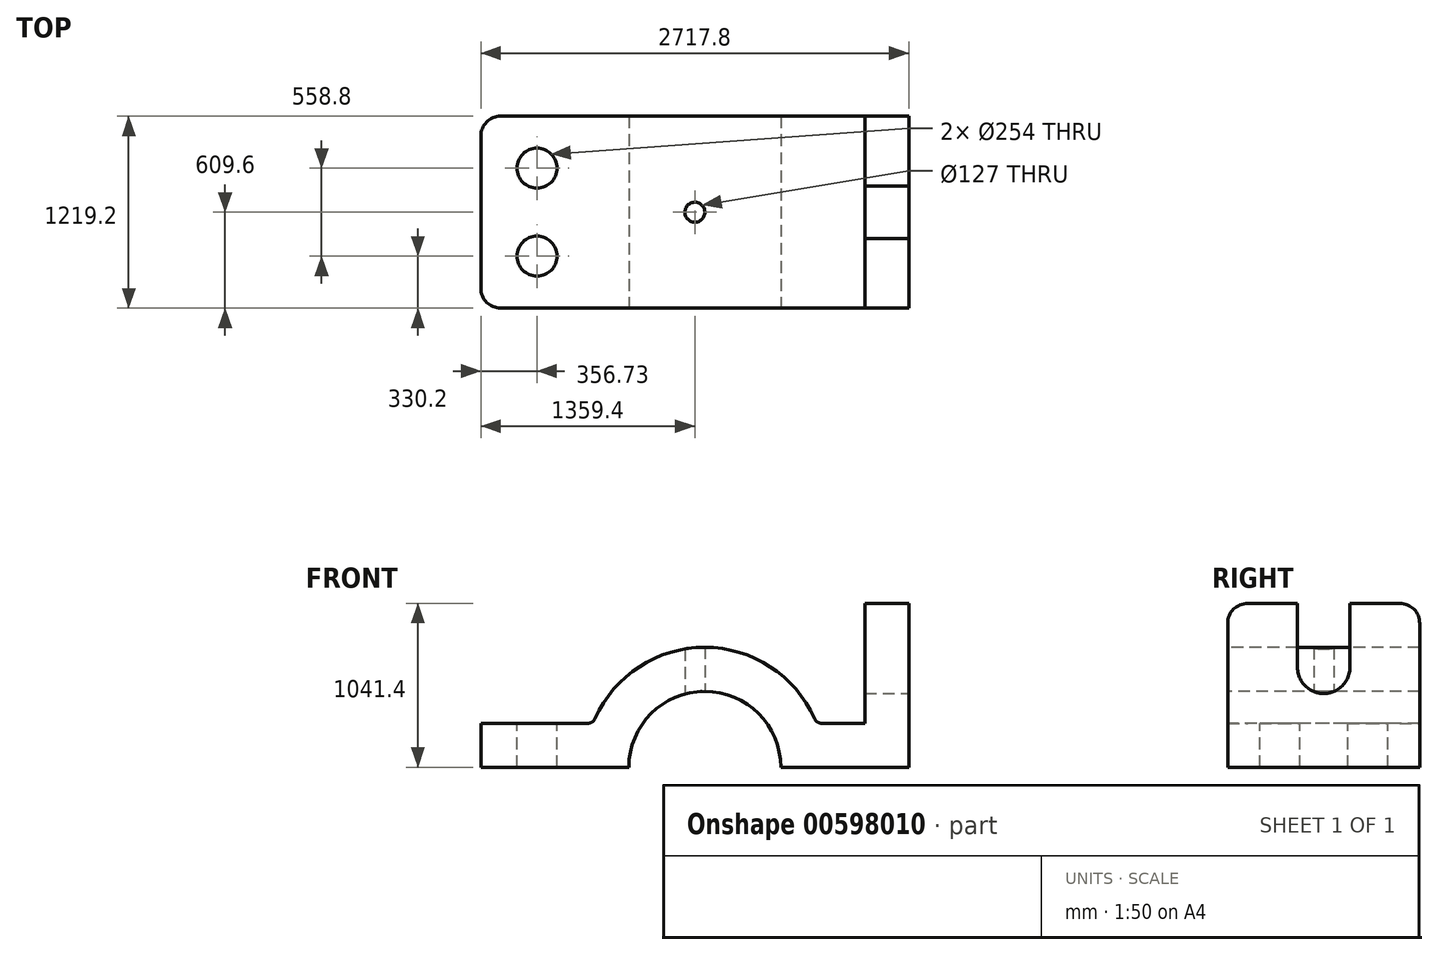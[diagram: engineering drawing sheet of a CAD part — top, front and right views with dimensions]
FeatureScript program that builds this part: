
annotation { "Feature Type Name" : "Feature", "Feature Type Description" : "" }
export const myFeature = defineFeature(function(context is Context, id is Id, definition is map)
    precondition{}
    {
        {
            var Q0;
            Q0=qCreatedBy(makeId("Front.planeOp"),FACE);
            var sketch = newSketch(context, id + "F0", { "sketchPlane" : qUnion([Q0])});
            skLineSegment(sketch, "E0.bottom", {"start": v(-1359.4, -709.05) * mm, "end": v(-419.6, -709.05) * mm});
            skLineSegment(sketch, "E0.top", {"start": v(1079, 332.35) * mm, "end": v(1358.4, 332.35) * mm});
            skLineSegment(sketch, "E0.left", {"start": v(-1359.4, -709.05) * mm, "end": v(-1359.4, -429.65) * mm});
            skLineSegment(sketch, "E0.right", {"start": v(1358.4, -709.05) * mm, "end": v(1358.4, 332.35) * mm});
            skLineSegment(sketch, "E1", {"start": v(1358.4, 332.35) * mm, "end": v(1079, 332.35) * mm});
            skLineSegment(sketch, "E2", {"start": v(1079, 332.35) * mm, "end": v(1079, -429.65) * mm});
            skLineSegment(sketch, "E3", {"start": v(1358.4, -709.05) * mm, "end": v(545.6, -709.05) * mm});
            skArc(sketch, "E4", {"start": v(545.6, -709.05) * mm, "mid": v(63, -226.45) * mm, "end": v(-419.6, -709.05) * mm});
            skArc(sketch, "E5", {"start": v(771.93, -429.65) * mm, "mid": v(63, 52.95) * mm, "end": v(-645.93, -429.65) * mm});
            skLineSegment(sketch, "E6", {"start": v(-1359.4, -429.65) * mm, "end": v(-645.93, -429.65) * mm});
            skLineSegment(sketch, "E7.trimOffspring", {"start": v(771.93, -429.65) * mm, "end": v(1079, -429.65) * mm});
            skSolve(sketch);
        }
        {
            var Q0;
            Q0=makeQuery(id+"F0.imprint","IMPRINT",FACE,{"disambiguationData":[TD([[makeQuery(id+"F0.imprint","IMPRINT",EDGE,{"derivedFrom":sQuery(id+"F0.wireOp",EDGE,"E0.bottom")}),1.0]])]});
            extrude(context, id + "F1", {"entities" : qUnion([Q0]), "endBound" : BoundingType.SYMMETRIC, "oppositeDirection" : true, "depth" : 1219.2 * mm, "offsetDistance" : 25.4 * mm});
        }
        {
            var Q0;
            Q0=makeQuery(id+"F1.opExtrude","SWEPT_FACE",FACE,{"disambiguationData":[OSD([sQuery(id+"F0.wireOp",EDGE,"E0.right")])]});
            var sketch = newSketch(context, id + "F2", { "sketchPlane" : qUnion([Q0])});
            skLineSegment(sketch, "E8", {"start": v(609.6, -709.05) * mm, "end": v(609.6, -74.05) * mm});
            skArc(sketch, "E9", {"start": v(-166.34, -74.05) * mm, "mid": v(0, -240.4) * mm, "end": v(166.34, -74.05) * mm});
            skLineSegment(sketch, "E10", {"start": v(166.34, -74.05) * mm, "end": v(166.34, 332.35) * mm});
            skLineSegment(sketch, "E11", {"start": v(-166.34, -74.05) * mm, "end": v(-166.34, 332.35) * mm});
            skLineSegment(sketch, "E12", {"start": v(-166.34, 332.35) * mm, "end": v(166.34, 332.35) * mm});
            skSolve(sketch);
        }
        {
            var Q0;
            Q0=makeQuery(id+"F2.imprint","IMPRINT",FACE,{"disambiguationData":[TD([[makeQuery(id+"F2.imprint","IMPRINT",EDGE,{"derivedFrom":sQuery(id+"F2.wireOp",EDGE,"E9")}),1.0]])]});
            extrude(context, id + "F3", {"entities" : qUnion([Q0]), "operationType" : NewBodyOperationType.REMOVE, "oppositeDirection" : true, "depth" : 279.4 * mm, "offsetDistance" : 25.4 * mm});
        }
        {
            var Q0;
            Q0=makeQuery(id+"F1.opExtrude","CAP_EDGE",EDGE,{"disambiguationData":[OSD([sQuery(id+"F0.wireOp",EDGE,"E0.top")])],"isStart":true});
            fillet(context, id + "F4", {"entities" : qUnion([Q0]), "radius" : 127 * mm, "tangentPropagation" : true, "allowEdgeOverflow" : false});
        }
        {
            var Q0;
            Q0=makeQuery(id+"F1.opExtrude","CAP_EDGE",EDGE,{"disambiguationData":[OSD([sQuery(id+"F0.wireOp",EDGE,"E0.top")])],"isStart":false});
            fillet(context, id + "F5", {"entities" : qUnion([Q0]), "radius" : 127 * mm, "tangentPropagation" : true, "allowEdgeOverflow" : false});
        }
        {
            var Q0;
            Q0=makeQuery(id+"F1.opExtrude","SWEPT_FACE",FACE,{"disambiguationData":[OSD([sQuery(id+"F0.wireOp",EDGE,"E6")])]});
            var sketch = newSketch(context, id + "F6", { "sketchPlane" : qUnion([Q0])});
            skCircle(sketch, "E13", {"center": v(0, 0) * mm, "radius": 63.5 * mm});
            skCircle(sketch, "E14", {"center": v(-1002.67, 279.4) * mm, "radius": 127 * mm});
            skCircle(sketch, "E15", {"center": v(-1002.67, -279.4) * mm, "radius": 127 * mm});
            skSolve(sketch);
        }
        {
            var Q0;
            Q0=makeQuery(id+"F6.imprint","IMPRINT",FACE,{"disambiguationData":[TD([[makeQuery(id+"F6.imprint","IMPRINT",EDGE,{"derivedFrom":sQuery(id+"F6.wireOp",EDGE,"E15")}),1.0]])]});
            extrude(context, id + "F7", {"entities" : qUnion([Q0]), "operationType" : NewBodyOperationType.REMOVE, "oppositeDirection" : true, "depth" : 279.4 * mm, "offsetDistance" : 25.4 * mm});
        }
        {
            var Q0;
            Q0=makeQuery(id+"F6.imprint","IMPRINT",FACE,{"disambiguationData":[TD([[makeQuery(id+"F6.imprint","IMPRINT",EDGE,{"derivedFrom":sQuery(id+"F6.wireOp",EDGE,"E14")}),1.0]])]});
            extrude(context, id + "F8", {"entities" : qUnion([Q0]), "operationType" : NewBodyOperationType.REMOVE, "oppositeDirection" : true, "depth" : 279.4 * mm, "offsetDistance" : 25.4 * mm});
        }
        {
            var Q0;
            Q0=sQuery(id+"F6.wireOp",VERTEX,"E13.center");
            var Q1;
            Q1=makeQuery(id+"F1.opExtrude","SWEPT_BODY",BODY,{"disambiguationData":[OSD([sQuery(id+"F0.wireOp",EDGE,"E0.bottom"),sQuery(id+"F0.wireOp",EDGE,"E0.right"),sQuery(id+"F0.wireOp",EDGE,"E0.top"),sQuery(id+"F0.wireOp",EDGE,"E2"),sQuery(id+"F0.wireOp",EDGE,"E3"),sQuery(id+"F0.wireOp",EDGE,"E4"),sQuery(id+"F0.wireOp",EDGE,"E5"),sQuery(id+"F0.wireOp",EDGE,"E0.left"),sQuery(id+"F0.wireOp",EDGE,"E6"),sQuery(id+"F0.wireOp",EDGE,"E7.trimOffspring")])]});
            hole(context, id + "F9", {"style" : HoleStyle.SIMPLE, "endStyle" : HoleEndStyle.BLIND, "oppositeDirection" : true, "holeDiameter" : 127 * mm, "majorDiameter" : 6.35 * mm, "holeDepth" : 279.4 * mm, "isTappedThrough" : true, "tappedDepth" : 12.7 * mm, "tapClearance" : 3, "locations" : qUnion([Q0]), "scope" : qUnion([Q1])});
        }
        {
            var Q0;
            Q0=makeQuery(id+"F1.opExtrude","CAP_EDGE",EDGE,{"disambiguationData":[OSD([sQuery(id+"F0.wireOp",EDGE,"E0.left")])],"isStart":false});
            var Q1;
            Q1=makeQuery(id+"F1.opExtrude","CAP_EDGE",EDGE,{"disambiguationData":[OSD([sQuery(id+"F0.wireOp",EDGE,"E0.left")])],"isStart":true});
            fillet(context, id + "F10", {"entities" : qUnion([Q0, Q1]), "radius" : 127 * mm, "tangentPropagation" : true, "allowEdgeOverflow" : false});
        }
        {
            var Q0;
            Q0=makeQuery(id+"F1.opExtrude","SWEPT_EDGE",EDGE,{"disambiguationData":[OSD([sQuery(id+"F0.wireOp",EDGE,"E5"),sQuery(id+"F0.wireOp",EDGE,"E6")])]});
            var Q1;
            Q1=makeQuery(id+"F1.opExtrude","SWEPT_EDGE",EDGE,{"disambiguationData":[OSD([sQuery(id+"F0.wireOp",EDGE,"E5"),sQuery(id+"F0.wireOp",EDGE,"E7.trimOffspring")])]});
            fillet(context, id + "F11", {"entities" : qUnion([Q0, Q1]), "radius" : 50.8 * mm, "tangentPropagation" : true, "allowEdgeOverflow" : false});
        }
    });
